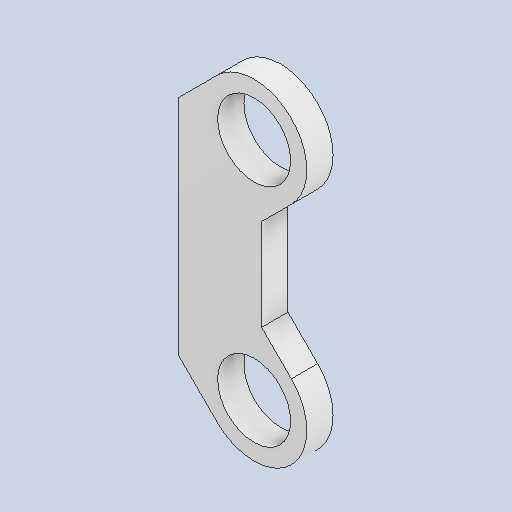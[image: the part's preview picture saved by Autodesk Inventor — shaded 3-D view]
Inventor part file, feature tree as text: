
AUTODESK INVENTOR PART (.ipt)
format: ipt  version: 2024.2 (Build 282272000, 272)  size: 277,504 bytes
history: native  units: in
note: dims shown in document units (in); Inventor stores cm internally (conversion verified against a paired STEP export)
features: extrude x1, sketch x1, other x1
ambient origin geometry x8: Origin, YZ Plane, XZ Plane, XY Plane, X Axis, Y Axis, Z Axis, Center Point
bodies: Solid1 (feature_tree)
feature tree (3):
  extrude  "Extrusion1"  [1 undecoded]
  sketch  "Sketch1"  dims[d0=0.0in d1=0.0in]
  other  "Saliente-Extruir3"
note: 1 required parameter value undecoded (feature->parameter linkage not recoverable at this tier; creation-order binding heuristic only, values carry confidence <= 0.55)
